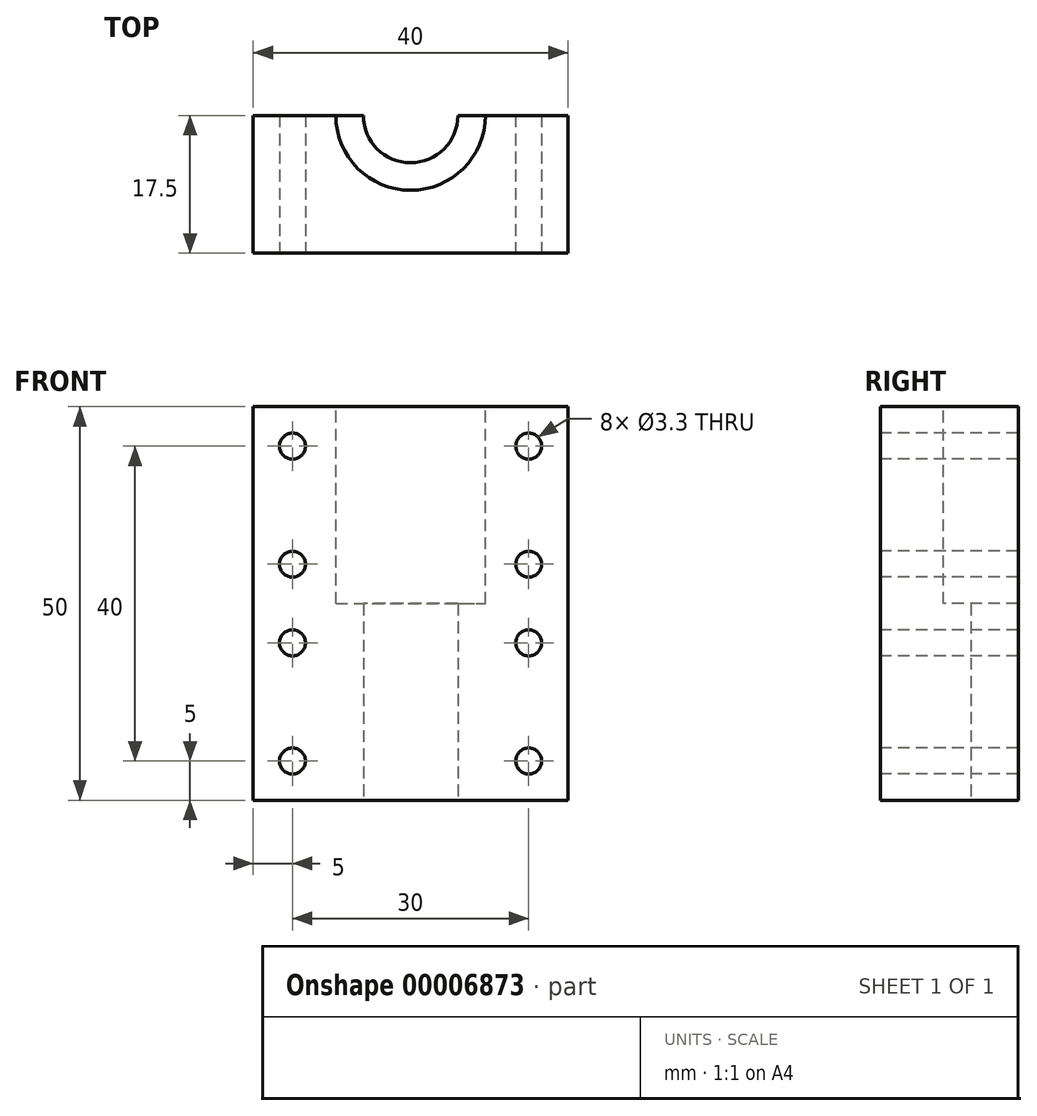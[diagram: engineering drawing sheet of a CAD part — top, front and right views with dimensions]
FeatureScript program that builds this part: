
annotation { "Feature Type Name" : "Feature", "Feature Type Description" : "" }
export const myFeature = defineFeature(function(context is Context, id is Id, definition is map)
    precondition{}
    {
        {
            var Q0;
            Q0=qCreatedBy(makeId("Top.planeOp"),FACE);
            var sketch = newSketch(context, id + "F0", { "sketchPlane" : qUnion([Q0])});
            skLineSegment(sketch, "E0.bottom", {"start": v(-20, 0) * mm, "end": v(20, 0) * mm});
            skLineSegment(sketch, "E0.top", {"start": v(-20, -17.5) * mm, "end": v(20, -17.5) * mm});
            skLineSegment(sketch, "E0.left", {"start": v(-20, 0) * mm, "end": v(-20, -17.5) * mm});
            skLineSegment(sketch, "E0.right", {"start": v(20, 0) * mm, "end": v(20, -17.5) * mm});
            skSolve(sketch);
        }
        {
            var Q0;
            Q0 = qSketchRegion(id + "F0", true);
            extrude(context, id + "F1", {"entities" : qUnion([Q0]), "depth" : (50) * mm});
        }
        {
            var Q0;
            Q0=makeQuery(id+"F1.opExtrude","CAP_FACE",FACE,{"disambiguationData":[OSD([sQuery(id+"F0.wireOp",EDGE,"E0.bottom"),sQuery(id+"F0.wireOp",EDGE,"E0.top"),sQuery(id+"F0.wireOp",EDGE,"E0.left"),sQuery(id+"F0.wireOp",EDGE,"E0.right")])],"isStart":false});
            var sketch = newSketch(context, id + "F2", { "sketchPlane" : qUnion([Q0])});
            skCircle(sketch, "E1", {"center": v(0, 0) * mm, "radius": 9.5 * mm});
            skSolve(sketch);
        }
        {
            var Q0;
            Q0 = qSketchRegion(id + "F2", true);
            extrude(context, id + "F3", {"entities" : qUnion([Q0]), "operationType" : NewBodyOperationType.REMOVE, "oppositeDirection" : true, "depth" : 25 * mm});
        }
        {
            var Q0;
            Q0=makeQuery(id+"F1.opExtrude","CAP_FACE",FACE,{"disambiguationData":[OSD([sQuery(id+"F0.wireOp",EDGE,"E0.bottom"),sQuery(id+"F0.wireOp",EDGE,"E0.top"),sQuery(id+"F0.wireOp",EDGE,"E0.left"),sQuery(id+"F0.wireOp",EDGE,"E0.right")])],"isStart":true});
            var sketch = newSketch(context, id + "F4", { "sketchPlane" : qUnion([Q0])});
            skCircle(sketch, "E2", {"center": v(0, 0) * mm, "radius": 6 * mm});
            skSolve(sketch);
        }
        {
            var Q0;
            Q0 = qSketchRegion(id + "F4", true);
            extrude(context, id + "F5", {"entities" : qUnion([Q0]), "operationType" : NewBodyOperationType.REMOVE, "oppositeDirection" : true, "depth" : 25 * mm});
        }
        {
            var Q0;
            Q0=makeQuery(id+"F1.opExtrude","SWEPT_FACE",FACE,{"disambiguationData":[OSD([sQuery(id+"F0.wireOp",EDGE,"E0.top")])]});
            var sketch = newSketch(context, id + "F6", { "sketchPlane" : qUnion([Q0])});
            skLineSegment(sketch, "E3", {"start": v(-20, 25) * mm, "end": v(20, 25) * mm, "construction": true});
            skCircle(sketch, "E4", {"center": v(-15, 20) * mm, "radius": 1.65 * mm});
            skCircle(sketch, "E5", {"center": v(-15, 5) * mm, "radius": 1.65 * mm});
            skCircle(sketch, "E6", {"center": v(15, 20) * mm, "radius": 1.65 * mm});
            skCircle(sketch, "E7", {"center": v(15, 5) * mm, "radius": 1.65 * mm});
            skCircle(sketch, "E8", {"center": v(15, 30) * mm, "radius": 1.65 * mm});
            skCircle(sketch, "E9", {"center": v(-15, 30) * mm, "radius": 1.65 * mm});
            skCircle(sketch, "E10", {"center": v(-15, 45) * mm, "radius": 1.65 * mm});
            skCircle(sketch, "E11", {"center": v(15, 45) * mm, "radius": 1.65 * mm});
            skSolve(sketch);
        }
        {
            var Q0;
            Q0 = qSketchRegion(id + "F6", true);
            extrude(context, id + "F7", {"entities" : qUnion([Q0]), "operationType" : NewBodyOperationType.REMOVE, "endBound" : BoundingType.THROUGH_ALL, "oppositeDirection" : true, "depth" : 25 * mm});
        }
    });
